# Revit family: FT LED Secure_2020
name_source: partatom
category: Lighting Fixtures
units: mm (PartAtom-declared; Revit-internal decimal feet)

## family parameters
Always vertical = Yes
Cut with Voids When Loaded = No
Light Source = Yes
OmniClass Number = 23.80.70.00
OmniClass Title = Lighting
Part Type = Normal
Room Calculation Point = No
Round Connector Dimension = Use Diameter
Shared = No
Work Plane-Based = No

## types (12) — shared parameters
Chromatic Index = CR>80
Color Filter = 16777215
Description = https://www.airfal.com
Dimming Lamp Color Temperature Shift = <None>
EX Area = Ex II 3GD Ex nR IIC T6 Gc Ex tc IIIC T85 ºC Dc
Emergency system = Yes
Emit from Line Length = 609.6 mm  [stored 2 ft]
IK = IK10
IP = IP68-2
LED/FLUO = LED or fluorescent tube
MacAdam Ellipse = 3/4
Photobiological risk group = RG1
URL = https://www.airfal.com
Unify glade rating = UGR<19
Useful life = L70B50>50000
zero-valued in all types: Default Elevation

## per-type parameters (varying)
| type | L | Net output | Photometric Web File | Tilt Angle | Watts |
| LS113 | 727 mm  [stored 2.38517 ft] | 997 lm | LS113 LED SECURE 600 13W 1490 lm 3000K.IES | 60.00° | 13 W |
| LS114 | 727 mm  [stored 2.38517 ft] | 1037 lm | LS114 LED SECURE 600 13W 1550 lm 4000K.IES | 60.00° | 13 W |
| LS123 | 727 mm  [stored 2.38517 ft] | 1712 lm | LS123 LED SECURE 600 16W 2560 lm 3000K.IES | 60.00° | 16 W |
| LS124 | 727 mm  [stored 2.38517 ft] | 1786 lm | LS124 LED SECURE 600 16W 2670 lm 4000K.IES | 60.00° | 16 W |
| LS213 | 1337 mm  [stored 4.38648 ft] | 1993 lm | LS213 LED SECURE 1200 24W 2980 lm 3000K.IES | 60.00° | 24 W |
| LS214 | 1337 mm  [stored 4.38648 ft] | 2140 lm | LS214 LED SECURE 1200 24W 3200 lm 4000K.IES | 60.00° | 24 W |
| LS223 | 1337 mm  [stored 4.38648 ft] | 3423 lm | LS223 LED SECURE 1200 32W 5120 lm 3000K.IES | 60.00° | 32 W |
| LS224 | 1337 mm  [stored 4.38648 ft] | 3571 lm | LS224 LED SECURE 1200 32W 5340 lm 4000K.IES | 60.00° | 32 W |
| LS313 | 1637 mm  [stored 5.37073 ft] | 2488 lm | LS313 LED SECURE 1500 29W 3720 lm 3000K.IES | 60.00° | 29 W |
| LS314 | 1637 mm  [stored 5.37073 ft] | 2675 lm | LS314 LED SECURE 1500 29W 4000 lm 4000K.IES | 60.00° | 29 W |
| LS323 | 1637 mm  [stored 5.37073 ft] | 4220 lm | LS323 LED SECURE 1500 40W 6310 lm 3000K.IES | 60.00° | 40 W |
| LS324 | 1637 mm  [stored 5.37073 ft] | 4481 lm | LS324 LED SECURE 1500 40W 7070 lm 4000K.IES | 90.00° | 40 W |

note: [stored X ft] marks values corroborated as IEEE doubles in the binary element streams (Revit-internal decimal feet)

## geometry (parser evidence)
native form markers: Blend x8, Sweep x26
no freeform markers — native parametric forms only
